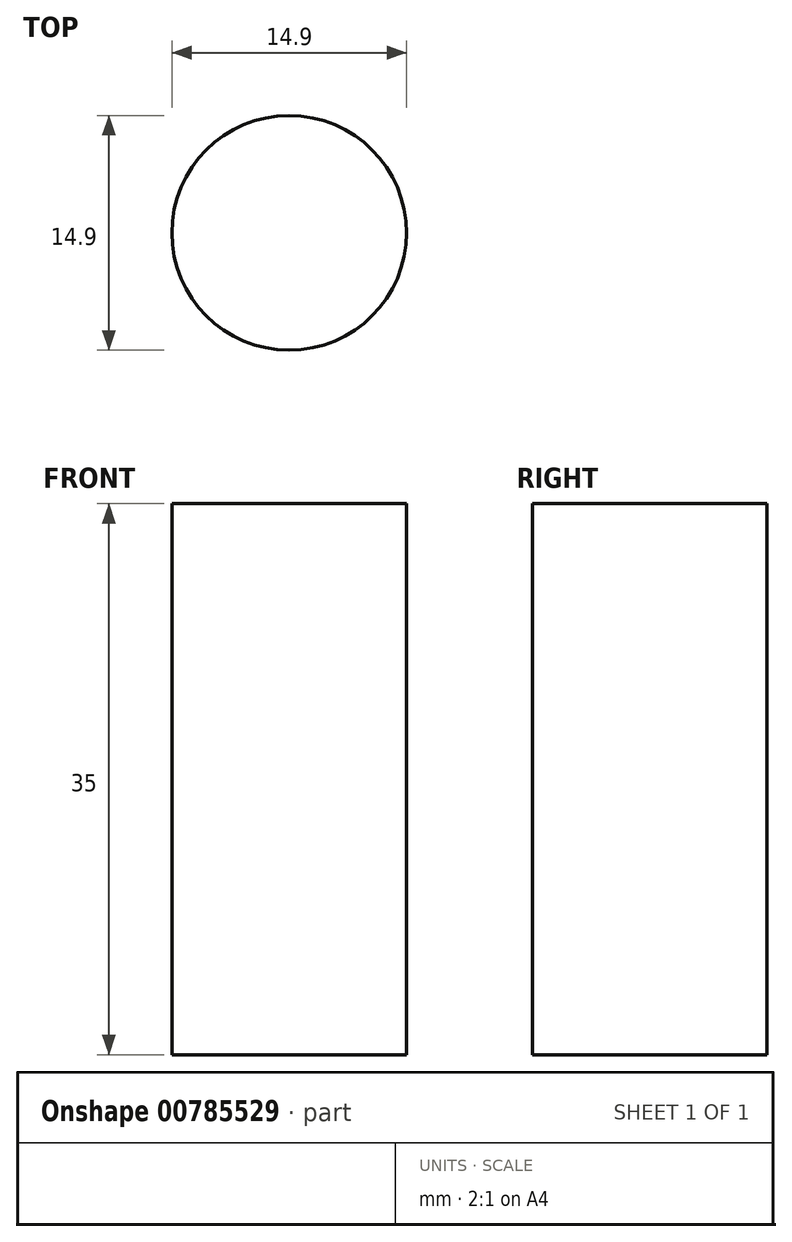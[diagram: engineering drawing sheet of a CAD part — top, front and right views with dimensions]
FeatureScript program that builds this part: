
annotation { "Feature Type Name" : "Feature", "Feature Type Description" : "" }
export const myFeature = defineFeature(function(context is Context, id is Id, definition is map)
    precondition{}
    {
        {
            var Q0;
            Q0=qCreatedBy(makeId("Top.planeOp"),FACE);
            var sketch = newSketch(context, id + "F0", { "sketchPlane" : qUnion([Q0])});
            skCircle(sketch, "E0", {"center": v(0, 0) * mm, "radius": 7.45 * mm});
            skSolve(sketch);
        }
        {
            var Q0;
            Q0 = qSketchRegion(id + "F0", true);
            extrude(context, id + "F1", {"entities" : qUnion([Q0]), "depth" : 35 * mm, "offsetDistance" : 25 * mm});
        }
    });
